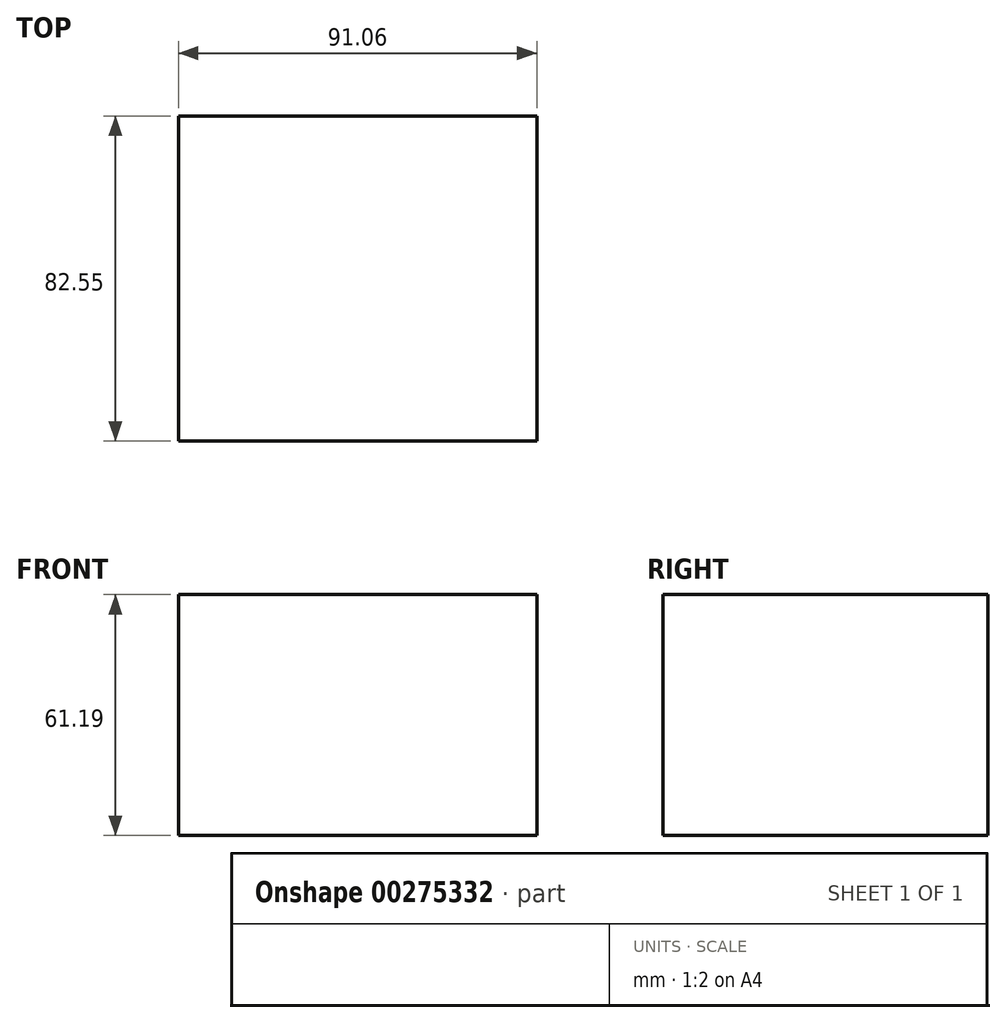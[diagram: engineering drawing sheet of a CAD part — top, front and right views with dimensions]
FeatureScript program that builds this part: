
annotation { "Feature Type Name" : "Feature", "Feature Type Description" : "" }
export const myFeature = defineFeature(function(context is Context, id is Id, definition is map)
    precondition{}
    {
        {
            var Q0;
            Q0=qCreatedBy(makeId("Front.planeOp"),FACE);
            var sketch = newSketch(context, id + "F0", { "sketchPlane" : qUnion([Q0])});
            skLineSegment(sketch, "E0.bottom", {"start": v(-36.22, 29.06) * mm, "end": v(54.84, 29.06) * mm});
            skLineSegment(sketch, "E0.top", {"start": v(-36.22, -32.13) * mm, "end": v(54.84, -32.13) * mm});
            skLineSegment(sketch, "E0.left", {"start": v(-36.22, 29.06) * mm, "end": v(-36.22, -32.13) * mm});
            skLineSegment(sketch, "E0.right", {"start": v(54.84, 29.06) * mm, "end": v(54.84, -32.13) * mm});
            skSolve(sketch);
        }
        {
            var Q0;
            Q0 = qSketchRegion(id + "F0", true);
            extrude(context, id + "F1", {"entities" : qUnion([Q0]), "depth" : 82.55 * mm});
        }
    });
